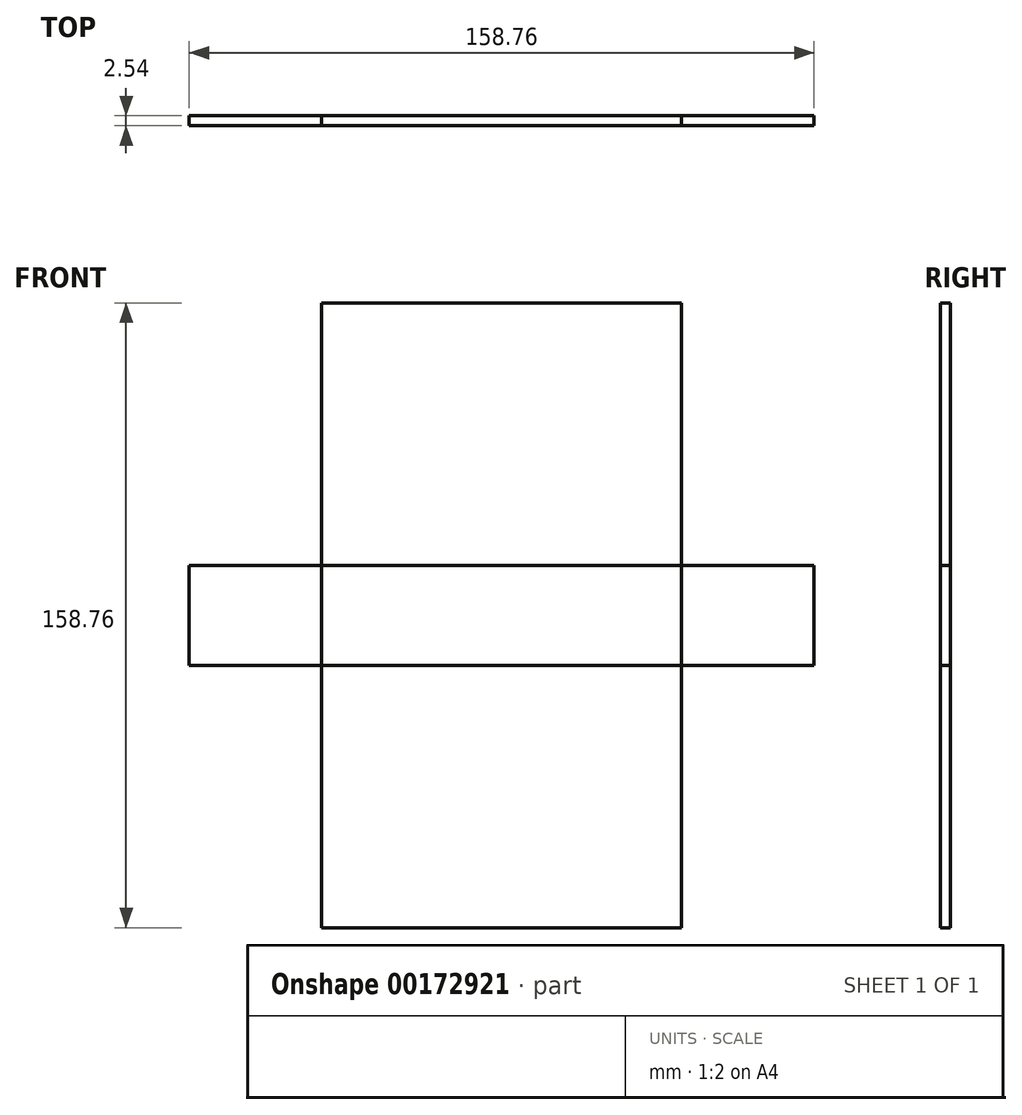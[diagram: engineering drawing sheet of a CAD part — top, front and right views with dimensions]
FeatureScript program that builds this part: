
annotation { "Feature Type Name" : "Feature", "Feature Type Description" : "" }
export const myFeature = defineFeature(function(context is Context, id is Id, definition is map)
    precondition{}
    {
        {
            var Q0;
            Q0=qCreatedBy(makeId("Front.planeOp"),FACE);
            var sketch = newSketch(context, id + "F0", { "sketchPlane" : qUnion([Q0])});
            skLineSegment(sketch, "E0.bottom", {"start": v(-79.38, 12.7) * mm, "end": v(79.38, 12.7) * mm});
            skLineSegment(sketch, "E0.top", {"start": v(-79.38, -12.7) * mm, "end": v(79.38, -12.7) * mm});
            skLineSegment(sketch, "E0.left", {"start": v(-79.38, 12.7) * mm, "end": v(-79.38, -12.7) * mm});
            skLineSegment(sketch, "E0.right", {"start": v(79.38, 12.7) * mm, "end": v(79.38, -12.7) * mm});
            skPoint(sketch, "E0.middle", {"position": v(0, 0) * mm});
            skSolve(sketch);
        }
        {
            var Q0;
            Q0=makeQuery(id+"F0.imprint","IMPRINT",FACE,{"disambiguationData":[TD([[makeQuery(id+"F0.imprint","IMPRINT",EDGE,{"derivedFrom":sQuery(id+"F0.wireOp",EDGE,"E0.bottom")}),-1.0]])]});
            extrude(context, id + "F1", {"entities" : qUnion([Q0]), "depth" : 2.54 * mm});
        }
        {
            var Q0;
            Q0=qCreatedBy(makeId("Front.planeOp"),FACE);
            var sketch = newSketch(context, id + "F2", { "sketchPlane" : qUnion([Q0])});
            skLineSegment(sketch, "E1.bottom", {"start": v(-79.38, -12.7) * mm, "end": v(79.38, -12.7) * mm});
            skLineSegment(sketch, "E1.top", {"start": v(-79.38, 12.7) * mm, "end": v(79.38, 12.7) * mm});
            skLineSegment(sketch, "E1.left", {"start": v(-79.38, -12.7) * mm, "end": v(-79.38, 12.7) * mm});
            skLineSegment(sketch, "E1.right", {"start": v(79.38, -12.7) * mm, "end": v(79.38, 12.7) * mm});
            skPoint(sketch, "E1.middle", {"position": v(0, 0) * mm});
            skSolve(sketch);
        }
        {
            var Q0;
            Q0=makeQuery(id+"F2.imprint","IMPRINT",FACE,{"disambiguationData":[TD([[makeQuery(id+"F2.imprint","IMPRINT",EDGE,{"derivedFrom":sQuery(id+"F2.wireOp",EDGE,"E1.bottom")}),1.0]])]});
            extrude(context, id + "F3", {"entities" : qUnion([Q0]), "depth" : 2.54 * mm});
        }
        {
            var Q0;
            Q0=qCreatedBy(makeId("Front.planeOp"),FACE);
            var sketch = newSketch(context, id + "F4", { "sketchPlane" : qUnion([Q0])});
            skLineSegment(sketch, "E2.bottom", {"start": v(45.72, -79.37) * mm, "end": v(-45.72, -79.37) * mm});
            skLineSegment(sketch, "E2.top", {"start": v(45.72, 79.38) * mm, "end": v(-45.72, 79.38) * mm});
            skLineSegment(sketch, "E2.left", {"start": v(45.72, -79.37) * mm, "end": v(45.72, 79.38) * mm});
            skLineSegment(sketch, "E2.right", {"start": v(-45.72, -79.37) * mm, "end": v(-45.72, 79.38) * mm});
            skPoint(sketch, "E2.middle", {"position": v(0, 0) * mm});
            skSolve(sketch);
        }
        {
            var Q0;
            Q0=makeQuery(id+"F4.imprint","IMPRINT",FACE,{"disambiguationData":[TD([[makeQuery(id+"F4.imprint","IMPRINT",EDGE,{"derivedFrom":sQuery(id+"F4.wireOp",EDGE,"E2.bottom")}),-1.0]])]});
            extrude(context, id + "F5", {"entities" : qUnion([Q0]), "depth" : 2.54 * mm});
        }
    });
